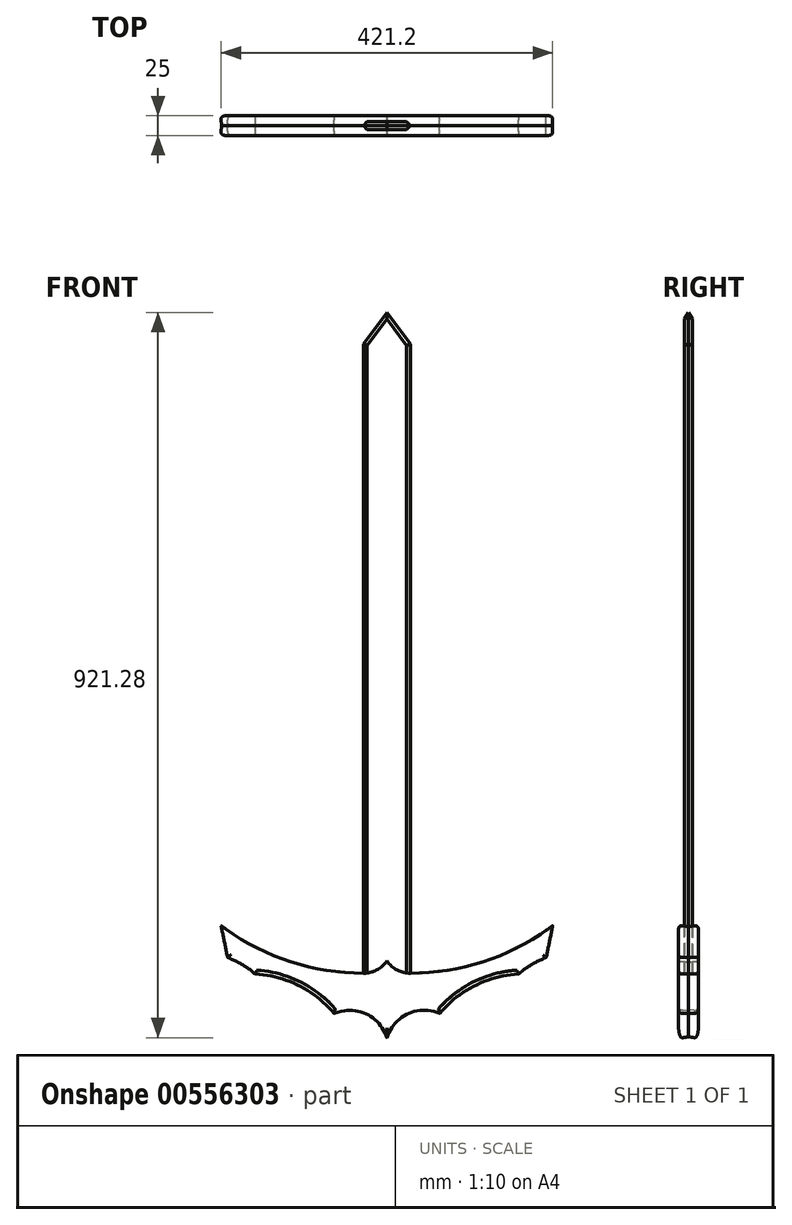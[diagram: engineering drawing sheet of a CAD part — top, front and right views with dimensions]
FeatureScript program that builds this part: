
annotation { "Feature Type Name" : "Feature", "Feature Type Description" : "" }
export const myFeature = defineFeature(function(context is Context, id is Id, definition is map)
    precondition{}
    {
        {
            var Q0;
            Q0=qCreatedBy(makeId("Front.planeOp"),FACE);
            var sketch = newSketch(context, id + "F0", { "sketchPlane" : qUnion([Q0])});
            skLineSegment(sketch, "E0", {"start": v(-30, 800) * mm, "end": v(-30, 0) * mm});
            skLineSegment(sketch, "E1", {"start": v(30, 800) * mm, "end": v(30, 0) * mm});
            skLineSegment(sketch, "E2", {"start": v(-30, 800) * mm, "end": v(30, 800) * mm, "construction": true});
            skLineSegment(sketch, "E3", {"start": v(0, 0) * mm, "end": v(0, 800) * mm, "construction": true});
            skLineSegment(sketch, "E4", {"start": v(-30, 800) * mm, "end": v(0, 840) * mm});
            skLineSegment(sketch, "E5", {"start": v(0, 840) * mm, "end": v(30, 800) * mm});
            skLineSegment(sketch, "E6", {"start": v(-30, 0) * mm, "end": v(30, 0) * mm});
            skSolve(sketch);
        }
        {
            var Q0;
            Q0=qCreatedBy(makeId("Front.planeOp"),FACE);
            var sketch = newSketch(context, id + "F1", { "sketchPlane" : qUnion([Q0])});
            skPoint(sketch, "E7.0", {"position": v(-30, 0) * mm});
            skPoint(sketch, "E8.0", {"position": v(30, 0) * mm});
            skPoint(sketch, "E9.0", {"position": v(0, 0) * mm});
            skLineSegment(sketch, "E10.0", {"start": v(-30, 0) * mm, "end": v(30, 0) * mm});
            skLineSegment(sketch, "E11.0", {"start": v(-30, 800) * mm, "end": v(-30, 0) * mm});
            skLineSegment(sketch, "E12.0", {"start": v(30, 800) * mm, "end": v(30, 0) * mm});
            skLineSegment(sketch, "E13.0", {"start": v(0, 0) * mm, "end": v(0, 800) * mm});
            skLineSegment(sketch, "E14.0", {"start": v(-30, 800) * mm, "end": v(0, 840) * mm});
            skLineSegment(sketch, "E15.0", {"start": v(0, 840) * mm, "end": v(30, 800) * mm});
            skLineSegment(sketch, "E16.0", {"start": v(-30, 800) * mm, "end": v(30, 800) * mm});
            skArc(sketch, "E17", {"start": v(30, 0) * mm, "mid": v(124.87, 15.4) * mm, "end": v(210, 60) * mm});
            skArc(sketch, "E18", {"start": v(-210, 60) * mm, "mid": v(-124.87, 15.4) * mm, "end": v(-30, 0) * mm});
            skArc(sketch, "E19", {"start": v(-30, 0) * mm, "mid": v(-13.23, 3.96) * mm, "end": v(0, 15) * mm});
            skArc(sketch, "E20", {"start": v(0, 15) * mm, "mid": v(13.23, 3.96) * mm, "end": v(30, 0) * mm});
            skLineSegment(sketch, "E21", {"start": v(-210, 60) * mm, "end": v(-202, 20.8) * mm});
            skLineSegment(sketch, "E22", {"start": v(210, 60) * mm, "end": v(202, 20.8) * mm});
            skArc(sketch, "E23", {"start": v(202, 20.8) * mm, "mid": v(183.51, 12.07) * mm, "end": v(167, 0) * mm});
            skArc(sketch, "E24", {"start": v(167, 0) * mm, "mid": v(111.8, -14.58) * mm, "end": v(67, -50) * mm});
            skArc(sketch, "E25", {"start": v(-167, 0) * mm, "mid": v(-183.51, 12.07) * mm, "end": v(-202, 20.8) * mm});
            skArc(sketch, "E26", {"start": v(-67, -50) * mm, "mid": v(-111.8, -14.58) * mm, "end": v(-167, 0) * mm});
            skArc(sketch, "E27", {"start": v(0, -80) * mm, "mid": v(-26.94, -50.35) * mm, "end": v(-67, -50) * mm});
            skArc(sketch, "E28", {"start": v(67, -50) * mm, "mid": v(26.94, -50.35) * mm, "end": v(0, -80) * mm});
            skSolve(sketch);
        }
        {
            var Q0;
            {var subQ0=sQuery(id+"F1.wireOp",EDGE,"E12.0");Q0=makeQuery(id+"F1.imprint","IMPRINT",FACE,{"disambiguationData":[TD([[makeQuery(id+"F1.imprint","IMPRINT",EDGE,{"derivedFrom":subQ0}),-1.0]])]});}
            var Q1;
            {var subQ0=sQuery(id+"F1.wireOp",EDGE,"E11.0");Q1=makeQuery(id+"F1.imprint","IMPRINT",FACE,{"disambiguationData":[TD([[makeQuery(id+"F1.imprint","IMPRINT",EDGE,{"derivedFrom":subQ0}),1.0]])]});}
            var Q2;
            {var subQ0=sQuery(id+"F1.wireOp",EDGE,"E14.0");Q2=makeQuery(id+"F1.imprint","IMPRINT",FACE,{"disambiguationData":[TD([[makeQuery(id+"F1.imprint","IMPRINT",EDGE,{"derivedFrom":subQ0}),-1.0]])]});}
            extrude(context, id + "F2", {"entities" : qUnion([Q0, Q1, Q2]), "endBound" : BoundingType.SYMMETRIC, "depth" : 10 * mm, "offsetDistance" : 25 * mm});
        }
        {
            var Q0;
            {var subQ3=sQuery(id+"F1.wireOp",EDGE,"E17");Q0=makeQuery(id+"F1.imprint","IMPRINT",FACE,{"disambiguationData":[TD([[makeQuery(id+"F1.imprint","IMPRINT",EDGE,{"derivedFrom":subQ3}),-1.0]])]});}
            var Q1;
            {var subQ0=sQuery(id+"F1.wireOp",EDGE,"E19");Q1=makeQuery(id+"F1.imprint","IMPRINT",FACE,{"disambiguationData":[TD([[makeQuery(id+"F1.imprint","IMPRINT",EDGE,{"derivedFrom":subQ0}),-1.0]])]});}
            var Q2;
            {var subQ0=sQuery(id+"F1.wireOp",EDGE,"E20");Q2=makeQuery(id+"F1.imprint","IMPRINT",FACE,{"disambiguationData":[TD([[makeQuery(id+"F1.imprint","IMPRINT",EDGE,{"derivedFrom":subQ0}),-1.0]])]});}
            extrude(context, id + "F3", {"entities" : qUnion([Q0, Q1, Q2]), "endBound" : BoundingType.SYMMETRIC, "depth" : 25 * mm, "offsetDistance" : 25 * mm, "hasDraft" : true, "draftAngle" : 3 * degree});
        }
        {
            var Q0;
            Q0=makeQuery(id+"F2.opExtrude","CAP_EDGE",EDGE,{"disambiguationData":[OSD([sQuery(id+"F1.wireOp",EDGE,"E11.0")])],"isStart":false});
            var Q1;
            Q1=makeQuery(id+"F2.opExtrude","CAP_EDGE",EDGE,{"disambiguationData":[OSD([sQuery(id+"F1.wireOp",EDGE,"E12.0")])],"isStart":false});
            var Q2;
            Q2=makeQuery(id+"F2.opExtrude","CAP_EDGE",EDGE,{"disambiguationData":[OSD([sQuery(id+"F1.wireOp",EDGE,"E11.0")])],"isStart":true});
            var Q3;
            Q3=makeQuery(id+"F2.opExtrude","CAP_EDGE",EDGE,{"disambiguationData":[OSD([sQuery(id+"F1.wireOp",EDGE,"E12.0")])],"isStart":true});
            chamfer(context, id + "F4", {"entities" : qUnion([Q0, Q1, Q2, Q3]), "width" : 5 * mm, "tangentPropagation" : true});
        }
        {
            var Q0;
            Q0=makeQuery(id+"F2.opExtrude","CAP_EDGE",EDGE,{"disambiguationData":[OSD([sQuery(id+"F1.wireOp",EDGE,"E15.0")])],"isStart":true});
            var Q1;
            Q1=makeQuery(id+"F2.opExtrude","CAP_EDGE",EDGE,{"disambiguationData":[OSD([sQuery(id+"F1.wireOp",EDGE,"E14.0")])],"isStart":true});
            var Q2;
            Q2=makeQuery(id+"F2.opExtrude","CAP_EDGE",EDGE,{"disambiguationData":[OSD([sQuery(id+"F1.wireOp",EDGE,"E14.0")])],"isStart":false});
            var Q3;
            Q3=makeQuery(id+"F2.opExtrude","CAP_EDGE",EDGE,{"disambiguationData":[OSD([sQuery(id+"F1.wireOp",EDGE,"E15.0")])],"isStart":false});
            chamfer(context, id + "F5", {"entities" : qUnion([Q0, Q1, Q2, Q3]), "width" : 5 * mm, "tangentPropagation" : true});
        }
        {
            var Q0;
            Q0=makeQuery(id+"F3.opExtrude","CAP_EDGE",EDGE,{"disambiguationData":[OSD([sQuery(id+"F1.wireOp",EDGE,"E26")])],"isStart":false});
            var Q1;
            Q1=makeQuery(id+"F3.opExtrude","CAP_EDGE",EDGE,{"disambiguationData":[OSD([sQuery(id+"F1.wireOp",EDGE,"E25")])],"isStart":false});
            var Q2;
            Q2=makeQuery(id+"F3.opExtrude","CAP_EDGE",EDGE,{"disambiguationData":[OSD([sQuery(id+"F1.wireOp",EDGE,"E27")])],"isStart":false});
            var Q3;
            Q3=makeQuery(id+"F3.opExtrude","CAP_EDGE",EDGE,{"disambiguationData":[OSD([sQuery(id+"F1.wireOp",EDGE,"E28")])],"isStart":false});
            var Q4;
            Q4=makeQuery(id+"F3.opExtrude","CAP_EDGE",EDGE,{"disambiguationData":[OSD([sQuery(id+"F1.wireOp",EDGE,"E24")])],"isStart":false});
            var Q5;
            Q5=makeQuery(id+"F3.opExtrude","CAP_EDGE",EDGE,{"disambiguationData":[OSD([sQuery(id+"F1.wireOp",EDGE,"E23")])],"isStart":false});
            var Q6;
            Q6=makeQuery(id+"F3.opExtrude","CAP_EDGE",EDGE,{"disambiguationData":[OSD([sQuery(id+"F1.wireOp",EDGE,"E25")])],"isStart":true});
            var Q7;
            Q7=makeQuery(id+"F3.opExtrude","CAP_EDGE",EDGE,{"disambiguationData":[OSD([sQuery(id+"F1.wireOp",EDGE,"E21")])],"isStart":true});
            var Q8;
            Q8=makeQuery(id+"F3.opExtrude","CAP_EDGE",EDGE,{"disambiguationData":[OSD([sQuery(id+"F1.wireOp",EDGE,"E26")])],"isStart":true});
            var Q9;
            Q9=makeQuery(id+"F3.opExtrude","CAP_EDGE",EDGE,{"disambiguationData":[OSD([sQuery(id+"F1.wireOp",EDGE,"E27")])],"isStart":true});
            var Q10;
            Q10=makeQuery(id+"F3.opExtrude","CAP_EDGE",EDGE,{"disambiguationData":[OSD([sQuery(id+"F1.wireOp",EDGE,"E28")])],"isStart":true});
            var Q11;
            Q11=makeQuery(id+"F3.opExtrude","CAP_EDGE",EDGE,{"disambiguationData":[OSD([sQuery(id+"F1.wireOp",EDGE,"E24")])],"isStart":true});
            var Q12;
            Q12=makeQuery(id+"F3.opExtrude","CAP_EDGE",EDGE,{"disambiguationData":[OSD([sQuery(id+"F1.wireOp",EDGE,"E23")])],"isStart":true});
            var Q13;
            Q13=makeQuery(id+"F3.opExtrude","CAP_EDGE",EDGE,{"disambiguationData":[OSD([sQuery(id+"F1.wireOp",EDGE,"E21")])],"isStart":false});
            var Q14;
            Q14=makeQuery(id+"F3.opExtrude","CAP_EDGE",EDGE,{"disambiguationData":[OSD([sQuery(id+"F1.wireOp",EDGE,"E22")])],"isStart":false});
            var Q15;
            Q15=makeQuery(id+"F3.opExtrude","CAP_EDGE",EDGE,{"disambiguationData":[OSD([sQuery(id+"F1.wireOp",EDGE,"E22")])],"isStart":true});
            fillet(context, id + "F6", {"entities" : qUnion([Q0, Q1, Q2, Q3, Q4, Q5, Q6, Q7, Q8, Q9, Q10, Q11, Q12, Q13, Q14, Q15]), "radius" : 5 * mm, "tangentPropagation" : true, "rho" : 0.5, "crossSection" : FilletCrossSection.CONIC, "allowEdgeOverflow" : false});
        }
    });
